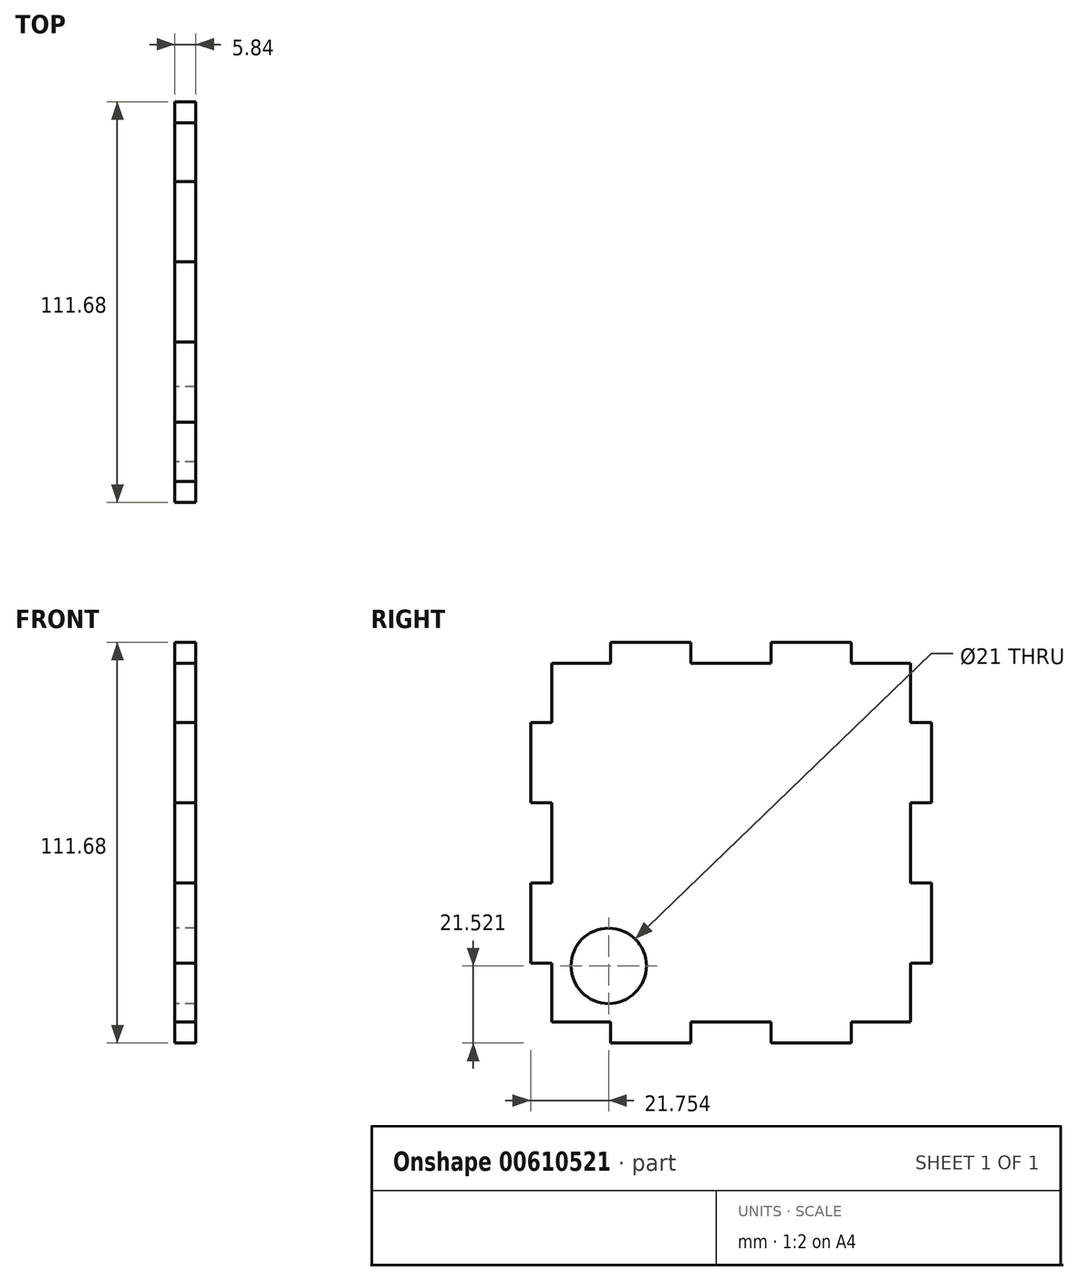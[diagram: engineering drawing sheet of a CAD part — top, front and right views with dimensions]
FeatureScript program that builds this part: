
annotation { "Feature Type Name" : "Feature", "Feature Type Description" : "" }
export const myFeature = defineFeature(function(context is Context, id is Id, definition is map)
    precondition{}
    {
        {
            var Q0;
            Q0=qCreatedBy(makeId("Right.planeOp"),FACE);
            var sketch = newSketch(context, id + "F0", { "sketchPlane" : qUnion([Q0])});
            skLineSegment(sketch, "E0.bottom", {"start": v(-50, 50) * mm, "end": v(50, 50) * mm});
            skLineSegment(sketch, "E0.top", {"start": v(-50, -50) * mm, "end": v(50, -50) * mm});
            skLineSegment(sketch, "E0.left", {"start": v(-50, 50) * mm, "end": v(-50, -50) * mm});
            skLineSegment(sketch, "E0.right", {"start": v(50, 50) * mm, "end": v(50, -50) * mm});
            skPoint(sketch, "E1.middle", {"position": v(0, 0) * mm});
            skLineSegment(sketch, "E2", {"start": v(-33.5, 50) * mm, "end": v(-33.5, 55.84) * mm});
            skLineSegment(sketch, "E3", {"start": v(-11.17, 50) * mm, "end": v(-11.17, 55.84) * mm});
            skPoint(sketch, "E3.endSnap0", {"position": v(0, 55.84) * mm});
            skLineSegment(sketch, "E4", {"start": v(11.17, 50) * mm, "end": v(11.17, 55.84) * mm});
            skLineSegment(sketch, "E5", {"start": v(33.5, 50) * mm, "end": v(33.5, 55.84) * mm});
            skLineSegment(sketch, "E6", {"start": v(-50, 33.5) * mm, "end": v(-55.84, 33.5) * mm});
            skLineSegment(sketch, "E7", {"start": v(-50, 11.17) * mm, "end": v(-55.84, 11.17) * mm});
            skLineSegment(sketch, "E8", {"start": v(-50, -11.17) * mm, "end": v(-55.84, -11.17) * mm});
            skLineSegment(sketch, "E9", {"start": v(-50, -33.5) * mm, "end": v(-55.84, -33.5) * mm});
            skLineSegment(sketch, "E10", {"start": v(-33.5, -50) * mm, "end": v(-33.5, -55.84) * mm});
            skLineSegment(sketch, "E11", {"start": v(-11.17, -50) * mm, "end": v(-11.17, -55.84) * mm});
            skLineSegment(sketch, "E12", {"start": v(11.17, -50) * mm, "end": v(11.17, -55.84) * mm});
            skLineSegment(sketch, "E13", {"start": v(33.5, -50) * mm, "end": v(33.5, -55.84) * mm});
            skLineSegment(sketch, "E14", {"start": v(50, -33.5) * mm, "end": v(55.84, -33.5) * mm});
            skLineSegment(sketch, "E15", {"start": v(50, -11.17) * mm, "end": v(55.84, -11.17) * mm});
            skLineSegment(sketch, "E16", {"start": v(50, 11.17) * mm, "end": v(55.84, 11.17) * mm});
            skLineSegment(sketch, "E17", {"start": v(50, 33.5) * mm, "end": v(55.84, 33.5) * mm});
            skLineSegment(sketch, "E18", {"start": v(55.84, 33.5) * mm, "end": v(55.84, 11.17) * mm});
            skLineSegment(sketch, "E19", {"start": v(55.84, -11.17) * mm, "end": v(55.84, -33.5) * mm});
            skLineSegment(sketch, "E20", {"start": v(11.17, -55.84) * mm, "end": v(33.5, -55.84) * mm});
            skLineSegment(sketch, "E21", {"start": v(-33.5, -55.84) * mm, "end": v(-11.17, -55.84) * mm});
            skLineSegment(sketch, "E22", {"start": v(-55.84, -33.5) * mm, "end": v(-55.84, -11.17) * mm});
            skLineSegment(sketch, "E23", {"start": v(-55.84, 33.5) * mm, "end": v(-55.84, 11.17) * mm});
            skLineSegment(sketch, "E24", {"start": v(-33.5, 55.84) * mm, "end": v(-11.17, 55.84) * mm});
            skLineSegment(sketch, "E25", {"start": v(11.17, 55.84) * mm, "end": v(33.5, 55.84) * mm});
            skPoint(sketch, "E1.left.start.orphan", {"position": v(-55.84, 55.84) * mm});
            skPoint(sketch, "E1.top.start.orphan", {"position": v(-55.84, -55.84) * mm});
            skPoint(sketch, "E26.trimOffspring.end.orphan", {"position": v(55.84, -55.84) * mm});
            skPoint(sketch, "E27.trimOffspring.end.orphan", {"position": v(55.84, 55.84) * mm});
            skCircle(sketch, "E28", {"center": v(-34.09, -34.32) * mm, "radius": 10.5 * mm});
            skSolve(sketch);
        }
        {
            var Q0;
            Q0=qSketchRegion(id+"F0",true);
            extrude(context, id + "F1", {"entities" : qUnion([Q0]), "depth" : 5.84 * mm, "offsetDistance" : 25 * mm});
        }
    });
